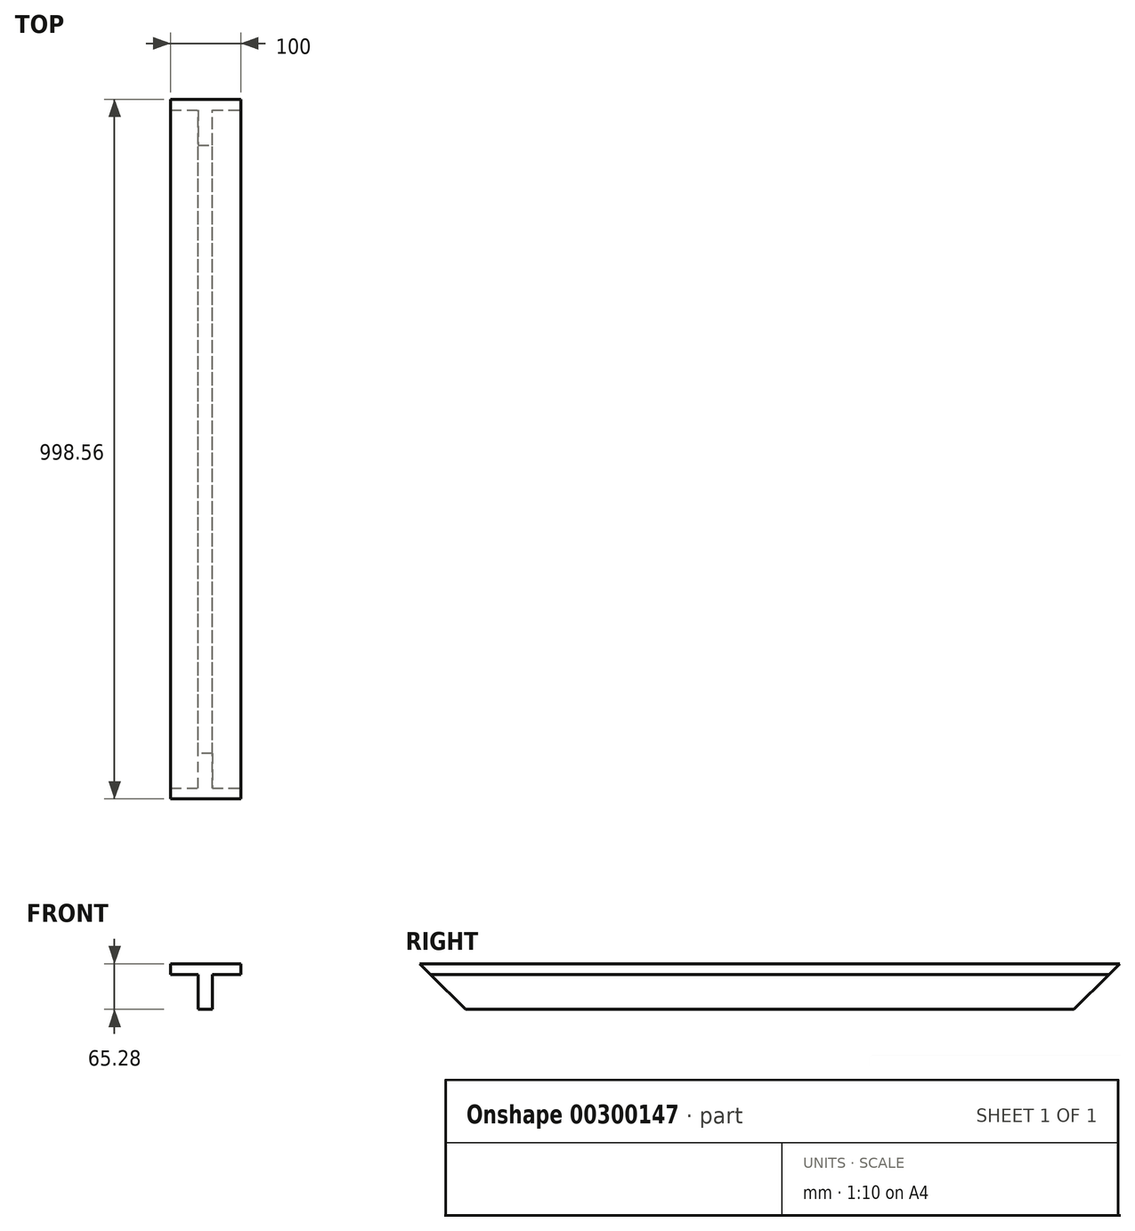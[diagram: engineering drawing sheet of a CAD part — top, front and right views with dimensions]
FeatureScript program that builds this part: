
annotation { "Feature Type Name" : "Feature", "Feature Type Description" : "" }
export const myFeature = defineFeature(function(context is Context, id is Id, definition is map)
    precondition{}
    {
        {
            var Q0;
            Q0=qCreatedBy(makeId("Front.planeOp"),FACE);
            var sketch = newSketch(context, id + "F0", { "sketchPlane" : qUnion([Q0])});
            skLineSegment(sketch, "E0.bottom", {"start": v(50, 7.64) * mm, "end": v(-50, 7.64) * mm});
            skLineSegment(sketch, "E0.top", {"start": v(50, -7.64) * mm, "end": v(-50, -7.64) * mm});
            skLineSegment(sketch, "E0.left", {"start": v(50, 7.64) * mm, "end": v(50, -7.64) * mm});
            skLineSegment(sketch, "E0.right", {"start": v(-50, 7.64) * mm, "end": v(-50, -7.64) * mm});
            skPoint(sketch, "E0.middle", {"position": v(0, 0) * mm});
            skLineSegment(sketch, "E1.bottom", {"start": v(0, -7.64) * mm, "end": v(9.43, -7.64) * mm});
            skLineSegment(sketch, "E2.MirrorCS", {"start": v(-1.13, -7.64) * mm, "end": v(-10.57, -7.64) * mm});
            skLineSegment(sketch, "E3.bottom", {"start": v(9.43, -7.64) * mm, "end": v(-10.57, -7.64) * mm});
            skLineSegment(sketch, "E3.top", {"start": v(9.43, -57.64) * mm, "end": v(-10.57, -57.64) * mm});
            skLineSegment(sketch, "E3.left", {"start": v(9.43, -7.64) * mm, "end": v(9.43, -57.64) * mm});
            skLineSegment(sketch, "E3.right", {"start": v(-10.57, -7.64) * mm, "end": v(-10.57, -57.64) * mm});
            skSolve(sketch);
        }
        {
            var Q0;
            Q0=qSketchRegion(id+"F0",true);
            extrude(context, id + "F1", {"entities" : qUnion([Q0]), "endBound" : BoundingType.SYMMETRIC, "depth" : 1000 * mm});
        }
        {
            var Q0;
            Q0=makeQuery(id+"F1.opExtrude","CAP_EDGE",EDGE,{"disambiguationData":[OSD([sQuery(id+"F0.wireOp",EDGE,"E3.top")])],"isStart":true});
            chamfer(context, id + "F2", {"entities" : qUnion([Q0]), "width" : 66 * mm, "tangentPropagation" : true});
        }
        {
            var Q0;
            Q0=makeQuery(id+"F1.opExtrude","CAP_EDGE",EDGE,{"disambiguationData":[OSD([sQuery(id+"F0.wireOp",EDGE,"E3.top")])],"isStart":false});
            chamfer(context, id + "F3", {"entities" : qUnion([Q0]), "width" : 66 * mm, "tangentPropagation" : true});
        }
    });
